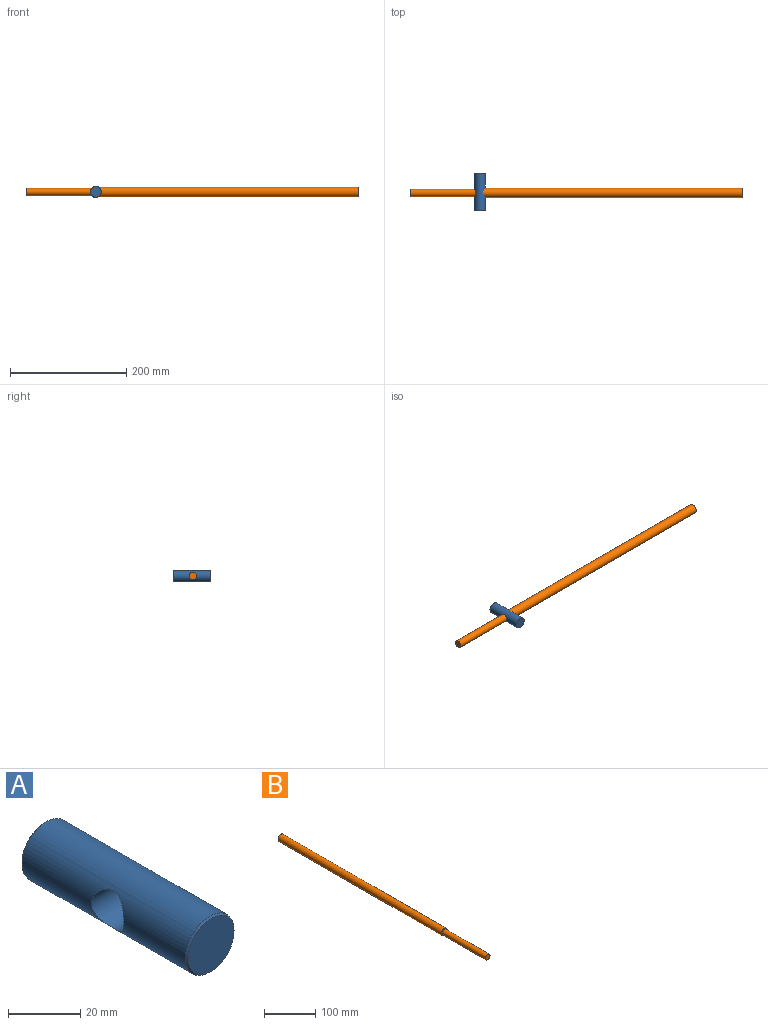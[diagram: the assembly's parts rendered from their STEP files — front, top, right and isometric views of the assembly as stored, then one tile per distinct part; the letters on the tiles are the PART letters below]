
ASSEMBLY  parts=2 mates=1
PART A: 6 faces, bbox 19x65x19 mm
  f0: cylinder r=9.5mm len=64mm, axis (0,1,0), area 3549.5mm2, adj f3,f4,f5
  f1: plane 18x18mm, normal (0,-1,0), area 254.5mm2, adj f5
  f2: plane 18x18mm, normal (0,1,0), area 254.5mm2, adj f4
  f3: cylinder r=6.35mm len=19mm, axis (1,0,0), area 664.5mm2, adj f0
  f4: cone r=9.5mm half-angle=45deg, axis (0,-1,0), area 41.1mm2, adj f0,f2
  f5: cone r=9mm half-angle=45deg, axis (0,1,0), area 41.1mm2, adj f0,f1
PART B: 5 faces, bbox 16x570x16 mm
  f0: plane 16x16mm, normal (0,1,0), area 201.1mm2, adj f1
  f1: cylinder r=8mm len=450mm, axis (0,1,0), area 22619.5mm2, adj f0,f2
  f2: plane 16x16mm, normal (0,-1,0), area 74.4mm2, adj f1,f3
  f3: cylinder r=6.35mm len=120mm, axis (0,1,0), area 4787.8mm2, adj f2,f4
  f4: plane 12.7x12.7mm, normal (0,-1,0), area 126.7mm2, adj f3
PLACE A t=(40.53,39.8,-24.15)mm
PLACE B rot(axis=(0.58,0.58,-0.58),120deg) t=(117.82,5.8,-24.15)mm
MATE revolute B.f1 <-> A.f3  axis (1,0,0) through (40.53,5.8,-24.15)mm
